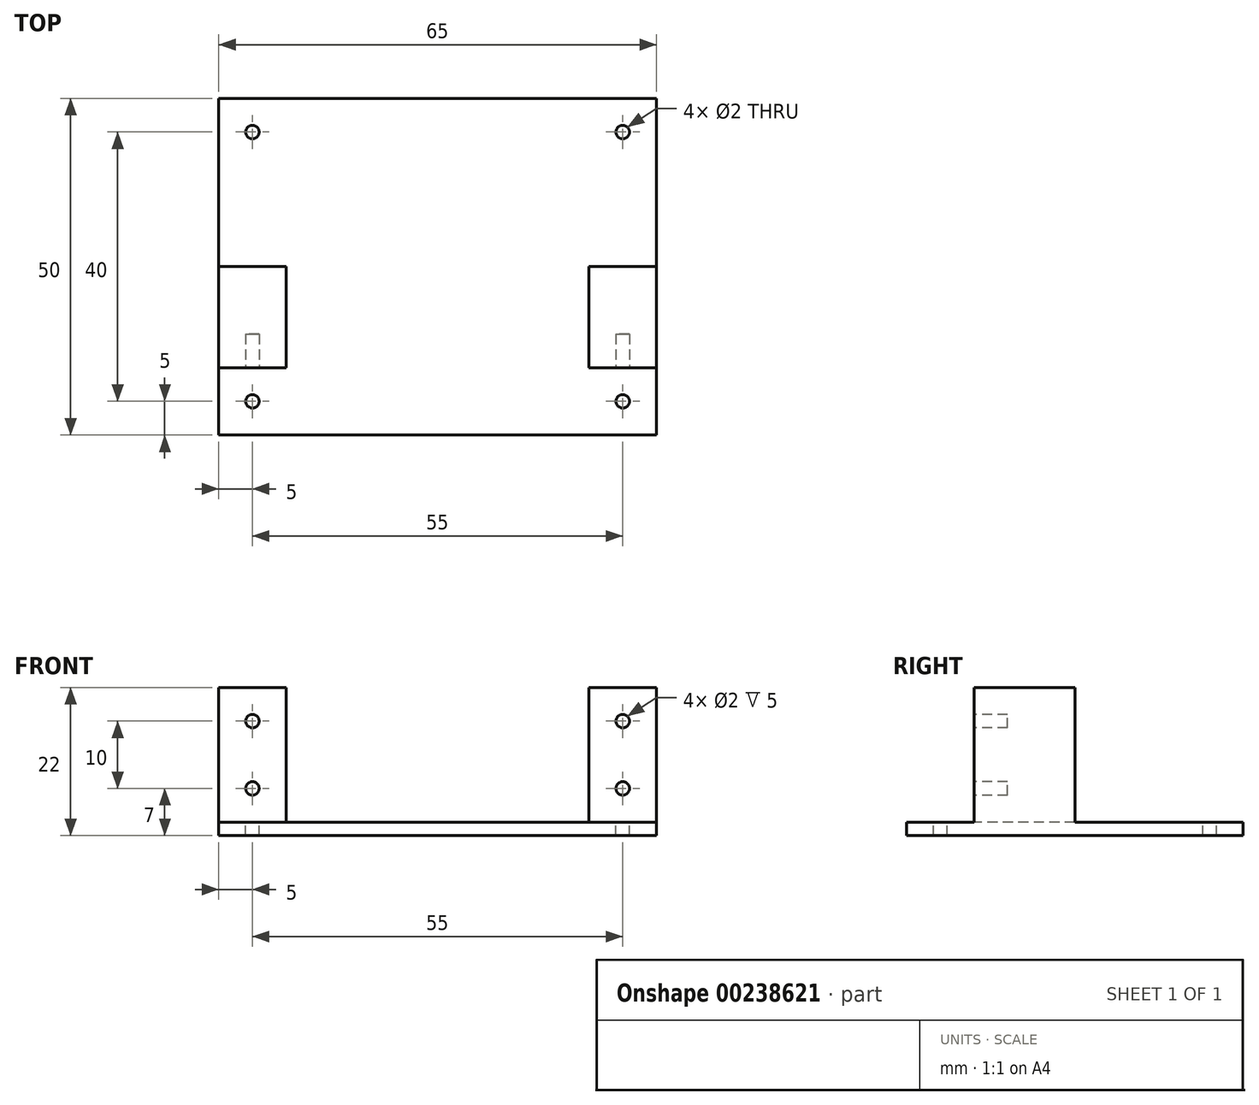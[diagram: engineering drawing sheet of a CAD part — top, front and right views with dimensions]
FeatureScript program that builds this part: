
annotation { "Feature Type Name" : "Feature", "Feature Type Description" : "" }
export const myFeature = defineFeature(function(context is Context, id is Id, definition is map)
    precondition{}
    {
        {
            var Q0;
            Q0=qCreatedBy(makeId("Top.planeOp"),FACE);
            var sketch = newSketch(context, id + "F0", { "sketchPlane" : qUnion([Q0])});
            skLineSegment(sketch, "E0", {"start": v(0, 0) * mm, "end": v(0, 50) * mm});
            skLineSegment(sketch, "E1", {"start": v(0, 50) * mm, "end": v(65, 50) * mm});
            skLineSegment(sketch, "E2", {"start": v(65, 50) * mm, "end": v(65, 0) * mm});
            skLineSegment(sketch, "E3", {"start": v(65, 0) * mm, "end": v(0, 0) * mm});
            skSolve(sketch);
        }
        {
            var Q0;
            Q0 = qSketchRegion(id + "F0", true);
            extrude(context, id + "F1", {"entities" : qUnion([Q0]), "depth" : 2 * mm});
        }
        {
            var Q0;
            Q0=makeQuery(id+"F1.opExtrude","CAP_FACE",FACE,{"disambiguationData":[OSD([sQuery(id+"F0.wireOp",EDGE,"E0"),sQuery(id+"F0.wireOp",EDGE,"E1"),sQuery(id+"F0.wireOp",EDGE,"E2"),sQuery(id+"F0.wireOp",EDGE,"E3")])],"isStart":false});
            var sketch = newSketch(context, id + "F2", { "sketchPlane" : qUnion([Q0])});
            skLineSegment(sketch, "E4", {"start": v(0, 0) * mm, "end": v(0, 10) * mm});
            skLineSegment(sketch, "E5", {"start": v(0, 10) * mm, "end": v(0, 25) * mm});
            skLineSegment(sketch, "E6", {"start": v(0, 25) * mm, "end": v(10, 25) * mm});
            skLineSegment(sketch, "E7", {"start": v(10, 25) * mm, "end": v(10, 10) * mm});
            skLineSegment(sketch, "E8", {"start": v(10, 10) * mm, "end": v(0, 10) * mm});
            skLineSegment(sketch, "E9", {"start": v(65, 0) * mm, "end": v(65, 25) * mm});
            skLineSegment(sketch, "E10", {"start": v(65, 25) * mm, "end": v(55, 25) * mm});
            skLineSegment(sketch, "E11", {"start": v(55, 25) * mm, "end": v(55, 10) * mm});
            skLineSegment(sketch, "E12", {"start": v(55, 10) * mm, "end": v(65, 10) * mm});
            skSolve(sketch);
        }
        {
            var Q0;
            Q0 = qSketchRegion(id + "F2", true);
            extrude(context, id + "F3", {"entities" : qUnion([Q0]), "operationType" : NewBodyOperationType.ADD, "depth" : 20 * mm});
        }
        {
            var Q0;
            Q0=makeQuery(id+"F3.opExtrude","SWEPT_FACE",FACE,{"disambiguationData":[OSD([sQuery(id+"F2.wireOp",EDGE,"E8")])]});
            var sketch = newSketch(context, id + "F4", { "sketchPlane" : qUnion([Q0])});
            skCircle(sketch, "E13", {"center": v(5, 17) * mm, "radius": 1 * mm});
            skCircle(sketch, "E14", {"center": v(5, 7) * mm, "radius": 1 * mm});
            skCircle(sketch, "E15", {"center": v(60, 17) * mm, "radius": 1 * mm});
            skCircle(sketch, "E16", {"center": v(60, 7) * mm, "radius": 1 * mm});
            skSolve(sketch);
        }
        {
            var Q0;
            Q0 = qSketchRegion(id + "F4", true);
            extrude(context, id + "F5", {"entities" : qUnion([Q0]), "operationType" : NewBodyOperationType.REMOVE, "oppositeDirection" : true, "depth" : 5 * mm});
        }
        {
            var Q0;
            Q0=makeQuery(id+"F1.opExtrude","CAP_FACE",FACE,{"disambiguationData":[OSD([sQuery(id+"F0.wireOp",EDGE,"E0"),sQuery(id+"F0.wireOp",EDGE,"E1"),sQuery(id+"F0.wireOp",EDGE,"E2"),sQuery(id+"F0.wireOp",EDGE,"E3")])],"isStart":false});
            var sketch = newSketch(context, id + "F6", { "sketchPlane" : qUnion([Q0])});
            skCircle(sketch, "E17", {"center": v(5, 45) * mm, "radius": 1 * mm});
            skCircle(sketch, "E18", {"center": v(60, 45) * mm, "radius": 1 * mm});
            skCircle(sketch, "E19", {"center": v(60, 5) * mm, "radius": 1 * mm});
            skCircle(sketch, "E20", {"center": v(5, 5) * mm, "radius": 1 * mm});
            skSolve(sketch);
        }
        {
            var Q0;
            Q0 = qSketchRegion(id + "F6", true);
            extrude(context, id + "F7", {"entities" : qUnion([Q0]), "operationType" : NewBodyOperationType.REMOVE, "oppositeDirection" : true, "depth" : 25 * mm});
        }
    });
